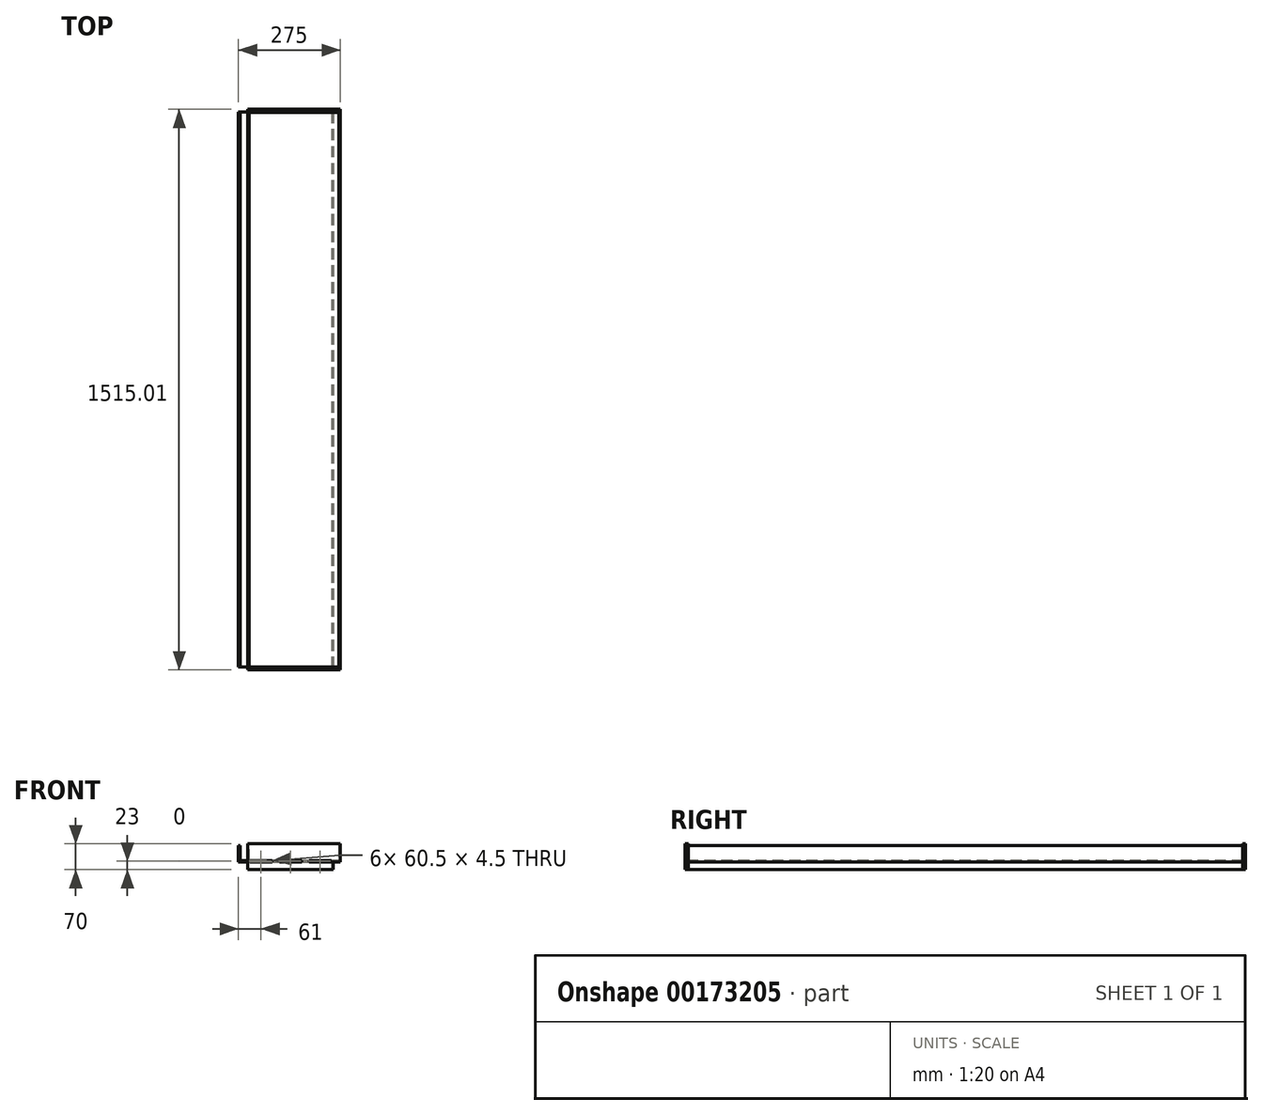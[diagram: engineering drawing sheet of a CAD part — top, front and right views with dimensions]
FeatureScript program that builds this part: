
annotation { "Feature Type Name" : "Feature", "Feature Type Description" : "" }
export const myFeature = defineFeature(function(context is Context, id is Id, definition is map)
    precondition{}
    {
        {
            var Q0;
            Q0=qCreatedBy(makeId("Front.planeOp"),FACE);
            var sketch = newSketch(context, id + "F0", { "sketchPlane" : qUnion([Q0])});
            skLineSegment(sketch, "E0", {"start": v(0, 44) * mm, "end": v(0, 0) * mm});
            skLineSegment(sketch, "E1", {"start": v(0, 0) * mm, "end": v(252, 0) * mm});
            skLineSegment(sketch, "E2", {"start": v(252, 0) * mm, "end": v(252, -20) * mm});
            skLineSegment(sketch, "E3", {"start": v(252, -20) * mm, "end": v(256, -20) * mm});
            skLineSegment(sketch, "E4", {"start": v(256, -20) * mm, "end": v(256, 0) * mm});
            skLineSegment(sketch, "E5", {"start": v(256, 0) * mm, "end": v(275, 0) * mm});
            skLineSegment(sketch, "E6", {"start": v(275, 4) * mm, "end": v(275, 0) * mm});
            skLineSegment(sketch, "E7", {"start": v(271, 4) * mm, "end": v(29, 4) * mm});
            skLineSegment(sketch, "E8", {"start": v(29, 4) * mm, "end": v(29, 44) * mm});
            skLineSegment(sketch, "E9", {"start": v(29, 44) * mm, "end": v(25, 44) * mm});
            skLineSegment(sketch, "E10", {"start": v(25, 44) * mm, "end": v(25, 4) * mm});
            skLineSegment(sketch, "E11", {"start": v(25, 4) * mm, "end": v(4, 4) * mm});
            skLineSegment(sketch, "E12", {"start": v(4, 4) * mm, "end": v(4, 44) * mm});
            skLineSegment(sketch, "E13", {"start": v(4, 44) * mm, "end": v(0, 44) * mm});
            skLineSegment(sketch, "E14", {"start": v(275, 4) * mm, "end": v(275, 44) * mm});
            skLineSegment(sketch, "E15", {"start": v(275, 44) * mm, "end": v(271, 44) * mm});
            skLineSegment(sketch, "E16", {"start": v(271, 44) * mm, "end": v(271, 4) * mm});
            skSolve(sketch);
        }
        {
            var Q0;
            Q0 = qSketchRegion(id + "F0", true);
            extrude(context, id + "F1", {"entities" : qUnion([Q0]), "oppositeDirection" : true, "depth" : 1500 * mm});
        }
        {
            var Q0;
            Q0=makeQuery(id+"F1.opExtrude","SWEPT_FACE",FACE,{"disambiguationData":[OSD([sQuery(id+"F0.wireOp",EDGE,"E1")])]});
            var sketch = newSketch(context, id + "F2", { "sketchPlane" : qUnion([Q0])});
            skLineSegment(sketch, "E17.bottom", {"start": v(91, 7) * mm, "end": v(31, 7) * mm});
            skLineSegment(sketch, "E17.top", {"start": v(91, 0) * mm, "end": v(31, 0) * mm});
            skLineSegment(sketch, "E17.left", {"start": v(91, 7) * mm, "end": v(91, 0) * mm});
            skLineSegment(sketch, "E17.right", {"start": v(31, 7) * mm, "end": v(31, 0) * mm});
            skLineSegment(sketch, "E18.1.0.0", {"start": v(171, 0) * mm, "end": v(111, 0) * mm});
            skLineSegment(sketch, "E18.1.0.1", {"start": v(171, 7) * mm, "end": v(111, 7) * mm});
            skLineSegment(sketch, "E18.1.0.2", {"start": v(111, 7) * mm, "end": v(111, 0) * mm});
            skLineSegment(sketch, "E18.1.0.3", {"start": v(171, 7) * mm, "end": v(171, 0) * mm});
            skLineSegment(sketch, "E18.2.0.0", {"start": v(251, 0) * mm, "end": v(191, 0) * mm});
            skLineSegment(sketch, "E18.2.0.1", {"start": v(251, 7) * mm, "end": v(191, 7) * mm});
            skLineSegment(sketch, "E18.2.0.2", {"start": v(191, 7) * mm, "end": v(191, 0) * mm});
            skLineSegment(sketch, "E18.2.0.3", {"start": v(251, 7) * mm, "end": v(251, 0) * mm});
            skLineSegment(sketch, "E18.direction1", {"start": v(31, 0) * mm, "end": v(111, 0) * mm, "construction": true});
            skLineSegment(sketch, "E19", {"start": v(0, -750) * mm, "end": v(450.44, -750) * mm, "construction": true});
            skPoint(sketch, "E19.endSnap0", {"position": v(0, -750) * mm});
            skLineSegment(sketch, "E20.MirrorCS", {"start": v(31, -1507) * mm, "end": v(31, -1500) * mm});
            skLineSegment(sketch, "E21.MirrorCS", {"start": v(111, -1507) * mm, "end": v(111, -1500) * mm});
            skLineSegment(sketch, "E22.MirrorCS", {"start": v(91, -1507) * mm, "end": v(91, -1500) * mm});
            skLineSegment(sketch, "E23.MirrorCS", {"start": v(251, -1507) * mm, "end": v(251, -1500) * mm});
            skLineSegment(sketch, "E24.MirrorCS", {"start": v(191, -1507) * mm, "end": v(191, -1500) * mm});
            skLineSegment(sketch, "E25.MirrorCS", {"start": v(171, -1507) * mm, "end": v(171, -1500) * mm});
            skLineSegment(sketch, "E26.MirrorCS", {"start": v(91, -1500) * mm, "end": v(31, -1500) * mm});
            skLineSegment(sketch, "E27.MirrorCS", {"start": v(91, -1507) * mm, "end": v(31, -1507) * mm});
            skLineSegment(sketch, "E28.MirrorCS", {"start": v(31, -1500) * mm, "end": v(111, -1500) * mm, "construction": true});
            skLineSegment(sketch, "E29.MirrorCS", {"start": v(251, -1507) * mm, "end": v(191, -1507) * mm});
            skLineSegment(sketch, "E30.MirrorCS", {"start": v(251, -1500) * mm, "end": v(191, -1500) * mm});
            skLineSegment(sketch, "E31.MirrorCS", {"start": v(171, -1507) * mm, "end": v(111, -1507) * mm});
            skLineSegment(sketch, "E32.MirrorCS", {"start": v(171, -1500) * mm, "end": v(111, -1500) * mm});
            skSolve(sketch);
        }
        {
            var Q0;
            Q0 = qSketchRegion(id + "F2", true);
            extrude(context, id + "F3", {"entities" : qUnion([Q0]), "operationType" : NewBodyOperationType.ADD, "oppositeDirection" : true, "depth" : 4 * mm});
        }
        {
            var Q0;
            Q0=makeQuery(id+"F3.opExtrude","SWEPT_FACE",FACE,{"disambiguationData":[OSD([sQuery(id+"F2.wireOp",EDGE,"E18.1.0.1")])]});
            var sketch = newSketch(context, id + "F4", { "sketchPlane" : qUnion([Q0])});
            skLineSegment(sketch, "E33", {"start": v(275, 0) * mm, "end": v(256, 0) * mm});
            skLineSegment(sketch, "E34", {"start": v(256, 0) * mm, "end": v(256, -21) * mm});
            skLineSegment(sketch, "E35", {"start": v(256, -21) * mm, "end": v(25, -21) * mm});
            skLineSegment(sketch, "E36", {"start": v(25, -21) * mm, "end": v(25, 49) * mm});
            skLineSegment(sketch, "E37", {"start": v(25, 49) * mm, "end": v(275, 49) * mm});
            skLineSegment(sketch, "E38", {"start": v(275, 49) * mm, "end": v(275, 0) * mm});
            skLineSegment(sketch, "E39.bottom", {"start": v(30.75, 4.25) * mm, "end": v(91.25, 4.25) * mm});
            skLineSegment(sketch, "E39.top", {"start": v(30.75, -0.25) * mm, "end": v(91.25, -0.25) * mm});
            skLineSegment(sketch, "E39.left", {"start": v(30.75, 4.25) * mm, "end": v(30.75, -0.25) * mm});
            skLineSegment(sketch, "E39.right", {"start": v(91.25, 4.25) * mm, "end": v(91.25, -0.25) * mm});
            skLineSegment(sketch, "E40.bottom", {"start": v(110.75, 4.25) * mm, "end": v(171.25, 4.25) * mm});
            skLineSegment(sketch, "E40.top", {"start": v(110.75, -0.25) * mm, "end": v(171.25, -0.25) * mm});
            skLineSegment(sketch, "E40.left", {"start": v(110.75, 4.25) * mm, "end": v(110.75, -0.25) * mm});
            skLineSegment(sketch, "E40.right", {"start": v(171.25, 4.25) * mm, "end": v(171.25, -0.25) * mm});
            skLineSegment(sketch, "E41.bottom", {"start": v(190.75, -0.25) * mm, "end": v(251.25, -0.25) * mm});
            skLineSegment(sketch, "E41.top", {"start": v(190.75, 4.25) * mm, "end": v(251.25, 4.25) * mm});
            skLineSegment(sketch, "E41.left", {"start": v(190.75, -0.25) * mm, "end": v(190.75, 4.25) * mm});
            skLineSegment(sketch, "E41.right", {"start": v(251.25, -0.25) * mm, "end": v(251.25, 4.25) * mm});
            skPoint(sketch, "E42", {"position": v(45, 24) * mm});
            skPoint(sketch, "E43", {"position": v(215, 24) * mm});
            skSolve(sketch);
        }
        {
            var Q0;
            Q0 = qSketchRegion(id + "F4", true);
            extrude(context, id + "F5", {"entities" : qUnion([Q0]), "depth" : 0.5 * mm, "hasSecondDirection" : true, "secondDirectionOppositeDirection" : true, "secondDirectionDepth" : 7.5 * mm});
        }
        {
            var Q0;
            Q0=makeQuery(id+"F5.opExtrude","SWEPT_BODY",BODY,{"disambiguationData":[OSD([sQuery(id+"F4.wireOp",EDGE,"E33"),sQuery(id+"F4.wireOp",EDGE,"E34"),sQuery(id+"F4.wireOp",EDGE,"E35"),sQuery(id+"F4.wireOp",EDGE,"E36"),sQuery(id+"F4.wireOp",EDGE,"E37"),sQuery(id+"F4.wireOp",EDGE,"E38"),sQuery(id+"F4.wireOp",EDGE,"E39.bottom"),sQuery(id+"F4.wireOp",EDGE,"E39.top"),sQuery(id+"F4.wireOp",EDGE,"E39.left"),sQuery(id+"F4.wireOp",EDGE,"E39.right"),sQuery(id+"F4.wireOp",EDGE,"E40.bottom"),sQuery(id+"F4.wireOp",EDGE,"E40.top"),sQuery(id+"F4.wireOp",EDGE,"E40.left"),sQuery(id+"F4.wireOp",EDGE,"E40.right"),sQuery(id+"F4.wireOp",EDGE,"E41.bottom"),sQuery(id+"F4.wireOp",EDGE,"E41.top"),sQuery(id+"F4.wireOp",EDGE,"E41.left"),sQuery(id+"F4.wireOp",EDGE,"E41.right")])]});
            transform(context, id + "F6", {"entities" : qUnion([Q0]), "transformType" : TransformType.TRANSLATION_3D, "dx" : 0 * mm, "dy" : 1507 * mm, "dz" : 0 * mm, "makeCopy" : true});
        }
    });
